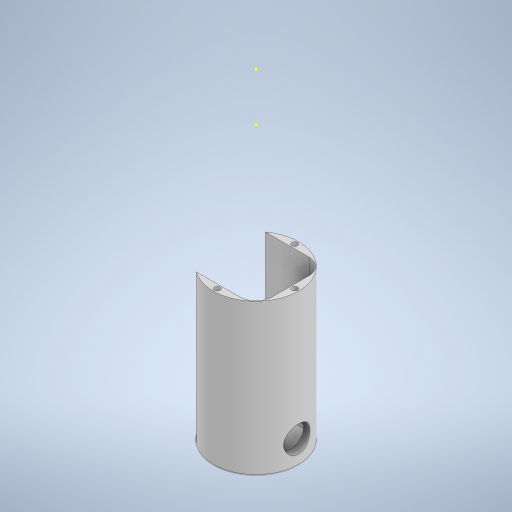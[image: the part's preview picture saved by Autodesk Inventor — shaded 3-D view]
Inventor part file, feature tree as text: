
AUTODESK INVENTOR PART (.ipt)
format: ipt  version: 2023 (Build 270158000, 158)  size: 2,000,384 bytes
history: native  units: in
note: dims shown in document units (in); Inventor stores cm internally (conversion verified against a paired STEP export)
features: extrude x44, sketch x38, projected_geometry x12, chamfer x8, other x6, fillet x6, mirror x3, pattern_circular x3, plane x2, helix x1
ambient origin geometry x8: Origin, YZ Plane, XZ Plane, XY Plane, X Axis, Y Axis, Z Axis, Center Point
bodies: Body1 (feature_tree), Body2 (feature_tree), Body3 (feature_tree), Body4 (feature_tree), Body5 (feature_tree)
feature tree (123):
  other  "BatteryCage"
  sketch  "Sketch1"  dims[d0=2.5748in d1=0.0098in]
  extrude  "Extrusion1"  Depth=0.0098in
  extrude  "Extrusion2"  Depth=0.4724in
  extrude  "Extrusion3"  Depth=0.0984in
  fillet  "Fillet1"  Radius=0.1969in
  chamfer  "Chamfer1"  Distance=0.0984in
  fillet  "Fillet2"  Radius=0.1181in
  extrude  "Extrusion4"  Depth=0.0197in
  chamfer  "Chamfer2"  Distance=0.0787in Angle=45.0deg
  sketch  "Sketch4"  dims[d4=0.0984in d5=0.0in d6=0.0079in d7=0.1969in]
  extrude  "Extrusion6"  Depth=4.4724in TaperAngle=0.0deg
  mirror  "Mirror1"
  sketch  "Sketch6"  dims[d9=0.1969in d10=0.0984in d11=0.0in d12=0.1181in]
  extrude  "Extrusion7"  Depth=0.0787in
  extrude  "Extrusion9"  Depth=0.5906in TaperAngle=0.0deg
  chamfer  "Chamfer4"  Distance=0.0984in
  sketch  "Sketch9"  dims[d19=0.1181in d20=4.4724in d21=0.0in]
  extrude  "Extrusion10"  Depth=0.0787in TaperAngle=45.0deg
  fillet  "Fillet3"  Radius=0.0984in
  extrude  "Extrusion11"  Depth=0.0984in
  extrude  "Extrusion12"  Depth=2.9528in TaperAngle=0.0deg
  sketch  "Sketch11"  dims[d31=0.1732in d32=0.5906in d33=0.0in]
  extrude  "Extrusion13"  Depth=0.5669in
  extrude  "Extrusion14"  Depth=0.8661in
  chamfer  "Chamfer5"  Distance=0.9843in
  extrude  "Extrusion15"  Depth=0.0787in TaperAngle=0.0deg
  extrude  "Extrusion16"  Depth=0.5906in
  sketch  "Sketch15"  dims[d36=0.0512in]
  extrude  "Extrusion17"  TaperAngle=0.0deg  [1 undecoded]
  extrude  "Extrusion18"  Depth=0.1122in
  extrude  "Extrusion19"  TaperAngle=0.0deg  [1 undecoded]
  pattern_circular  "Circular Pattern1"  Count=4 Angle=360.0deg
  extrude  "Extrusion20"  Depth=0.3937in TaperAngle=0.0deg
  pattern_circular  "Circular Pattern2"  Count=8 Angle=360.0deg
  sketch  "Sketch18"  dims[d41=0.1339in d42=0.0984in d43=0.0in]
  helix  "Coil1"  [1 undecoded]
  extrude  "Extrusion21"  Depth=0.3937in
  extrude  "Extrusion22"  Depth=0.3937in
  extrude  "Extrusion23"  Depth=0.0787in
  extrude  "Extrusion24"  Depth=0.3937in
  chamfer  "Chamfer6"  Distance=0.1457in
  extrude  "Sensor Tower Base"  Depth=0.3937in
  extrude  "Extrusion27"  Depth=0.3937in TaperAngle=0.0deg
  sketch  "Sketch23"  dims[d56=0.0in d57=0.8661in]
  extrude  "Extrusion28"  Depth=0.3937in
  sketch  "Sketch30"  dims[d63=0.2756in]
  extrude  "Extrusion34"  TaperAngle=0.0deg  [1 undecoded]
  extrude  "Extrusion35"  Depth=0.3937in TaperAngle=0.0deg
  extrude  "Extrusion36"  Depth=0.3937in
  extrude  "Extrusion44"  Depth=0.3937in
  extrude  "Extrusion37"  Depth=0.3937in TaperAngle=0.0deg
  extrude  "Extrusion38"  Depth=0.0787in TaperAngle=45.0deg
  mirror  "Mirror2"
  extrude  "Extrusion39"  Depth=0.315in
  extrude  "Extrusion40"  Depth=0.3937in
  extrude  "Extrusion41"  Depth=0.3937in
  mirror  "Mirror3"
  chamfer  "Chamfer9"  [1 undecoded]
  extrude  "Extrusion29"  Depth=0.3937in
  extrude  "Extrusion30"  Depth=0.3937in
  extrude  "Extrusion31"  Depth=0.3937in
  chamfer  "Chamfer7"  [1 undecoded]
  extrude  "Extrusion32"  Depth=0.3937in
  pattern_circular  "Circular Pattern3"  [2 undecoded]
  extrude  "O-ring Gland"  Depth=0.3937in
  fillet  "Fillet4"  Radius=0.1969in
  plane  "Work Plane2"
  extrude  "Extrusion47"  Depth=0.3937in
  chamfer  "Chamfer8"  [1 undecoded]
  extrude  "Start of Camera"  Depth=0.3937in
  fillet  "Fillet5"  Radius=0.0787in
  sketch  "Sketch37"  dims[d80=0.7087in]
  extrude  "Extrusion43"  Depth=0.3937in
  plane  "Work Plane1"
  extrude  "Extrusion45"  Depth=0.3937in
  extrude  "Extrusion46"  Depth=0.3937in
  fillet  "Fillet6"  Radius=0.1181in
  sketch  "Sketch3"  dims[d2=2.0512in d3=0.4724in]
  projected_geometry  "Projected Loop1"
  sketch  "Sketch5"  dims[d8=0.7874in]
  projected_geometry  "Projected Loop2"
  other  "StartOfPiCage"
  other  "PiCage"
  sketch  "Sketch8"  dims[d13=0.3937in d14=0.0in d15=0.0197in d16=0.0512in d17=0.0787in d18=45.0deg]
  projected_geometry  "Projected Loop3"
  sketch  "Sketch10"  dims[d22=0.0512in d23=0.0787in d24=45.0deg d25=0.0512in]
  sketch  "Sketch12"  dims[d34=0.0512in]
  sketch  "Sketch14"  dims[d35=0.0512in]
  projected_geometry  "Projected Loop4"
  sketch  "Sketch16"  dims[d37=0.0in]
  sketch  "Sketch17"  dims[d38=0.0512in]
  sketch  "Sketch19"  dims[d44=0.0512in d45=0.0787in d46=45.0deg d47=0.0984in]
  projected_geometry  "Projected Loop5"
  sketch  "Sketch20"  dims[d48=0.0984in d49=2.0472in]
  sketch  "Sketch21"  dims[d50=0.2756in d51=2.9528in d52=0.0in]
  other  "SensorTower"
  sketch  "Sketch22"  dims[d53=1.1811in d54=0.0in d55=0.5669in]
  sketch  "Sketch24"  dims[d58=0.0787in]
  projected_geometry  "Projected Loop6"
  other  "SensorCover"
  sketch  "Sketch25"  dims[d59=0.6299in]
  sketch  "Sketch26"  dims[d60=0.0984in]
  sketch  "Sketch27"  dims[d61=0.0in]
  sketch  "Sketch28"  dims[d62=0.1772in]
  sketch  "Sketch31"  dims[d64=0.0172in d65=0.9843in d66=0.0in]
  sketch  "Sketch32"  dims[d67=0.9843in d68=0.0787in d69=45.0deg d70=0.1969in d71=0.0in]
  sketch  "Sketch33"  dims[d72=0.7874in d73=0.5906in]
  projected_geometry  "Projected Loop7"
  sketch  "Sketch34"  dims[d74=0.5669in d75=0.0in]
  projected_geometry  "Projected Loop8"
  projected_geometry  "Projected Loop9"
  projected_geometry  "Projected Loop10"
  projected_geometry  "Projected Loop11"
  sketch  "Sketch35"  dims[d76=3.1181in d77=0.1122in]
  projected_geometry  "Projected Loop12"
  sketch  "Sketch36"  dims[d78=0.2756in d79=0.0in]
  other  "Camera"
  sketch  "Sketch38"  dims[d81=0.0in]
  sketch  "Sketch39"  dims[d82=0.1732in]
  sketch  "Sketch40"  dims[d83=1.4173in]
  sketch  "Sketch41"  dims[d84=0.2362in d85=0.0in d86=1.5748in d87=360.0deg]
  sketch  "Sketch43"  dims[d89=0.1575in d90=0.2756in d91=0.0in d92=3.1496in d93=360.0deg d95=2.4016in d96=0.185in d97=0.1102in d98=0.0787in d99=1.4016in d100=0.1457in d101=0.3937in d102=0.9449in d103=0.0in d104=90.0deg d105=90.0deg d106=0.0in d107=0.0in d108=0.3937in d109=0.0in d110=0.2362in d111=0.0in d112=0.3937in d113=0.0in d114=0.2756in d115=0.2756in d116=0.3937in d117=0.0in d118=0.0768in d119=0.0787in d120=45.0deg d122=0.315in d126=0.1417in d127=0.1181in d128=0.0in d129=2.126in d130=0.2953in d131=1.378in d132=0.0in d133=1.4961in d134=1.3386in d135=0.0709in d136=0.1969in d137=0.9843in d138=0.0in d139=0.2756in d140=0.0787in d141=2.126in d142=0.1969in d143=0.2756in d144=0.1181in d145=0.0in d146=0.1969in d147=1.378in d148=0.0in d149=1.2992in d150=0.1181in d151=0.0in d152=0.4134in d153=0.0787in d154=45.0deg d155=0.9449in d156=0.0787in d157=0.2362in d158=0.0in d159=2.3622in d160=360.0deg d162=1.4173in d163=0.1496in d164=0.0689in d165=0.0in d167=0.1181in d168=0.0787in d169=0.0787in d170=45.0deg d171=1.0079in d172=1.0in d173=0.0197in d174=0.0591in d175=0.0591in d176=0.3937in d177=0.0in d178=0.4724in d179=0.0in d180=0.0787in d181=0.0787in d182=0.4724in d183=0.0in d184=0.2756in d185=0.5118in d186=0.0in d187=45.0deg d188=0.0591in d189=0.5512in d190=0.0in d191=0.0472in d192=30.0deg d193=0.0315in d194=0.0787in d195=0.0787in d196=0.0in d197=0.5512in d198=1.2008in d199=0.0in d200=0.063in d201=45.0deg d202=30.0deg d203=0.1181in d204=0.0945in d205=1.2008in d206=0.0in d207=1.4961in d208=0.0984in d209=0.063in d210=0.0in d211=0.0394in d212=1.1772in d213=0.689in d214=0.0in d215=0.0276in d216=0.0in d217=0.0787in d218=0.1378in d219=0.3937in d220=0.126in d221=0.0in d222=0.7835in d223=0.3937in d224=0.0in d225=0.3858in d226=0.0787in d227=0.0787in d228=45.0deg d229=-0.0236in d230=0.1575in d231=0.748in d232=0.3937in d233=0.0in]
note: 9 required parameter values undecoded (feature->parameter linkage not recoverable at this tier; creation-order binding heuristic only, values carry confidence <= 0.55)
